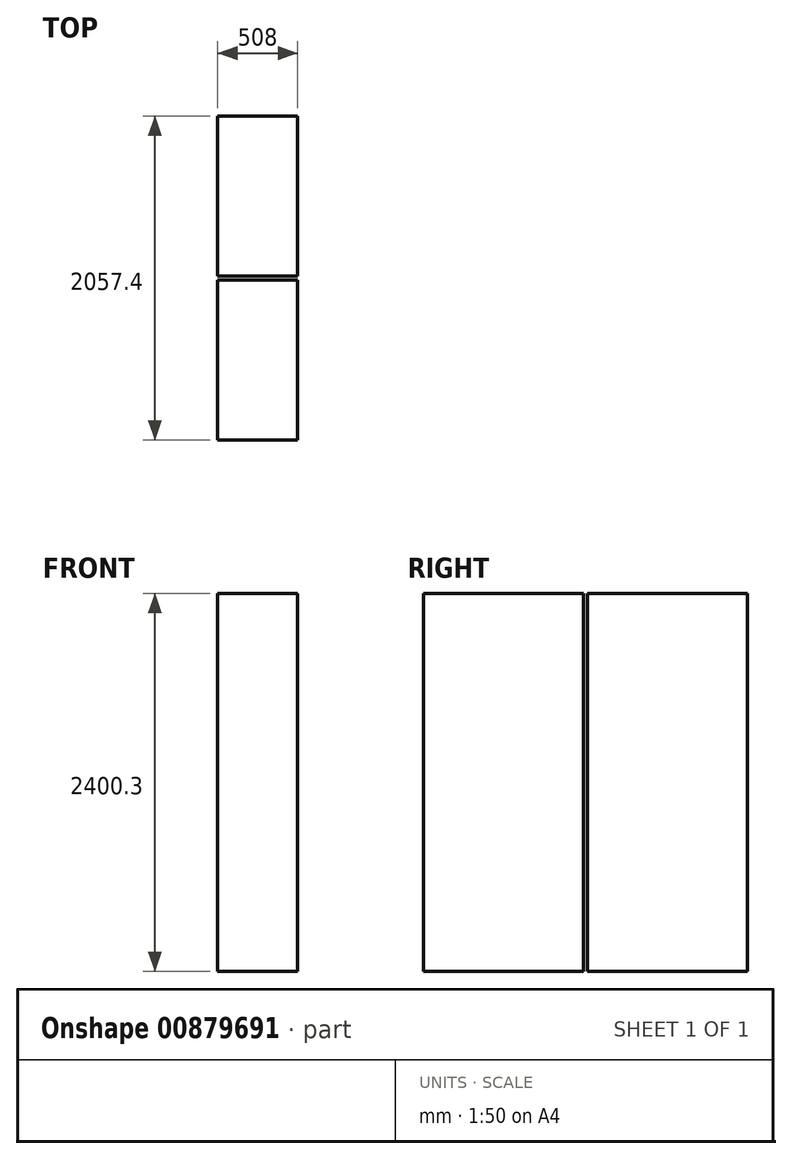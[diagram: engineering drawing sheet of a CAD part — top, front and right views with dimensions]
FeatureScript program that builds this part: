
annotation { "Feature Type Name" : "Feature", "Feature Type Description" : "" }
export const myFeature = defineFeature(function(context is Context, id is Id, definition is map)
    precondition{}
    {
        {
            var Q0;
            Q0=qCreatedBy(makeId("Top.planeOp"),FACE);
            var sketch = newSketch(context, id + "F0", { "sketchPlane" : qUnion([Q0])});
            skLineSegment(sketch, "E0.bottom", {"start": v(-251.7, 1393.62) * mm, "end": v(256.3, 1393.62) * mm});
            skLineSegment(sketch, "E0.top", {"start": v(-251.7, 377.62) * mm, "end": v(256.3, 377.62) * mm});
            skLineSegment(sketch, "E0.left", {"start": v(-251.7, 1393.62) * mm, "end": v(-251.7, 377.62) * mm});
            skLineSegment(sketch, "E0.right", {"start": v(256.3, 1393.62) * mm, "end": v(256.3, 377.62) * mm});
            skLineSegment(sketch, "E1.bottom", {"start": v(-251.7, 352.22) * mm, "end": v(256.3, 352.22) * mm});
            skLineSegment(sketch, "E1.top", {"start": v(-251.7, -663.78) * mm, "end": v(256.3, -663.78) * mm});
            skLineSegment(sketch, "E1.left", {"start": v(-251.7, 352.22) * mm, "end": v(-251.7, -663.78) * mm});
            skLineSegment(sketch, "E1.right", {"start": v(256.3, 352.22) * mm, "end": v(256.3, -663.78) * mm});
            skSolve(sketch);
        }
        {
            var Q0;
            Q0=makeQuery(id+"F0.imprint","IMPRINT",FACE,{"disambiguationData":[TD([[makeQuery(id+"F0.imprint","IMPRINT",EDGE,{"derivedFrom":sQuery(id+"F0.wireOp",EDGE,"E0.bottom")}),-1.0]])]});
            var Q1;
            Q1=makeQuery(id+"F0.imprint","IMPRINT",FACE,{"disambiguationData":[TD([[makeQuery(id+"F0.imprint","IMPRINT",EDGE,{"derivedFrom":sQuery(id+"F0.wireOp",EDGE,"E1.bottom")}),-1.0]])]});
            extrude(context, id + "F1", {"entities" : qUnion([Q0, Q1]), "depth" : 2400.3 * mm, "offsetDistance" : 25.4 * mm});
        }
    });
